FCSTD DOCUMENT  (FreeCAD 0.18R)
Label: Test-Alignment
License: All rights reserved
LicenseURL: http://en.wikipedia.org/wiki/All_rights_reserved
objects: App::DocumentObjectGroup×6, Points::Feature×1, Mesh::Feature×1, Part::Part2DObjectPython×1
note: 1 computed .brp shape members not serialized (recipe doc carries the construction recipe); baked Part::Feature solids carry a one-line shape summary decoded from their .brp

FEATURE [Points::Feature] Points
  Placement = pos=(507831,4273070,66.914) rot=(0,0,1;0rad)
FEATURE [App::DocumentObjectGroup] Point_Groups  label="Point Groups"
  Group = -> [Points]
FEATURE [Mesh::Feature] Surface
  Placement = pos=(507831,4.27302e+06,66.5716) rot=(0,0,1;0rad)
FEATURE [App::DocumentObjectGroup] Surfaces
  Group = -> [Surface]
FEATURE [App::DocumentObjectGroup] Contours
FEATURE [App::DocumentObjectGroup] ggg
FEATURE [App::DocumentObjectGroup] GuideLines  label="Guide Lines"
  Group = -> [ggg]
FEATURE [Part::Part2DObjectPython] Line001  # Draft 2D object (typed FeaturePython)
  ChamferSize = 0
  Closed = false
  End = (507828,4273075,70)
  FilletRadius = 0
  Length = 78.8972
  MakeFace = false
  Placement = pos=(507783,4273010,70) rot=(0,0,1;0rad)
  Points = (2) [(0,0,0),(44.7188,65,0)]
  Start = (507783,4273010,70)
  Subdivisions = 0
FEATURE [App::DocumentObjectGroup] Alignments
  Group = -> [GuideLines,Line001]
